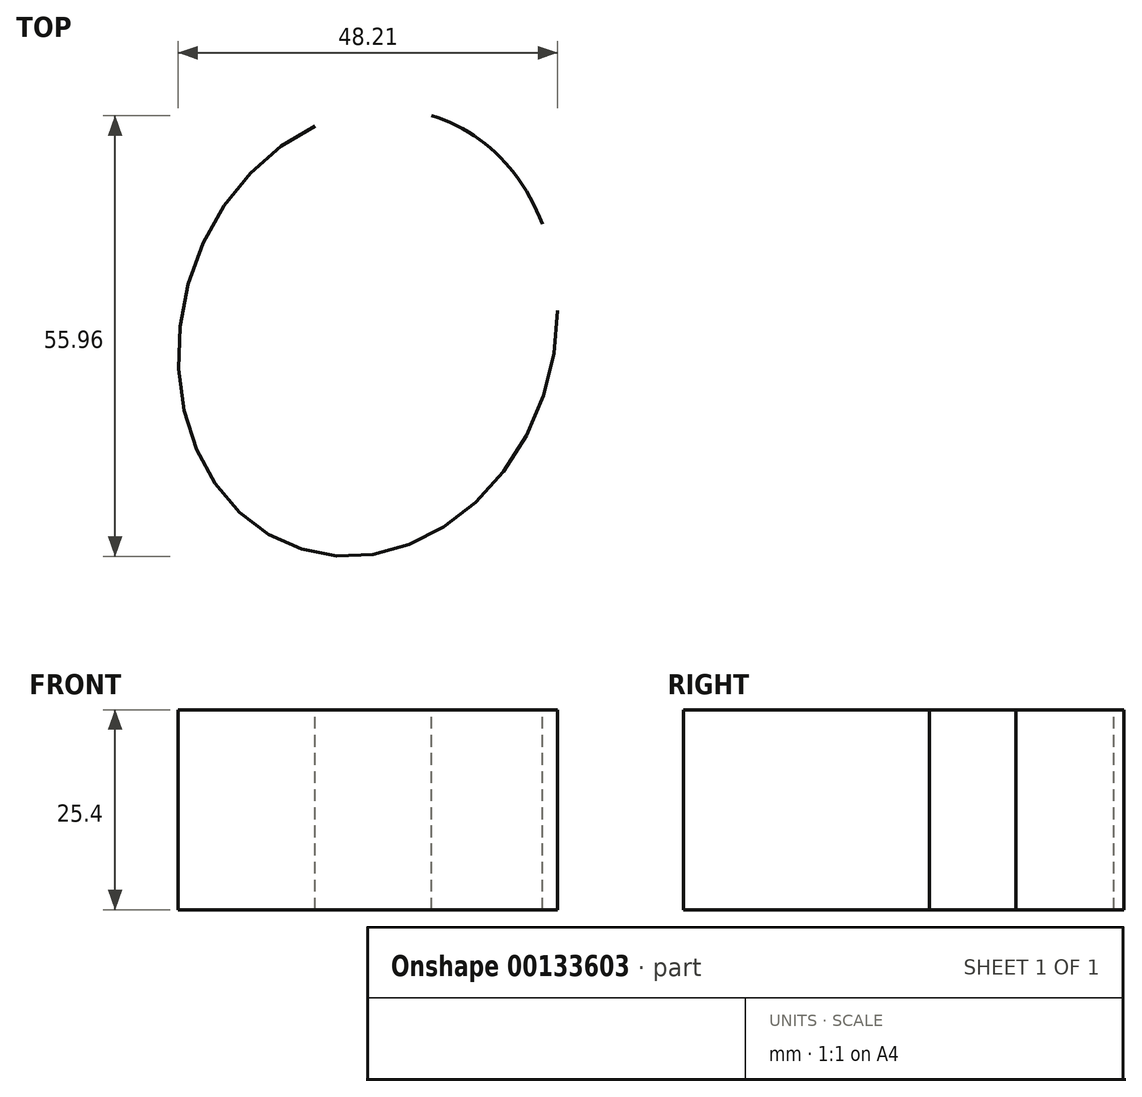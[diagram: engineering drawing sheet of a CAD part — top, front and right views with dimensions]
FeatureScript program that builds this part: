
annotation { "Feature Type Name" : "Feature", "Feature Type Description" : "" }
export const myFeature = defineFeature(function(context is Context, id is Id, definition is map)
    precondition{}
    {
        {
            var Q0;
            Q0=qCreatedBy(makeId("Top.planeOp"),FACE);
            var sketch = newSketch(context, id + "F0", { "sketchPlane" : qUnion([Q0])});
            skEllipticalArc(sketch, "E0", {});
            skPoint(sketch, "E1.2.internal.snap0", {"position": v(-56.5, -27.58) * mm});
            skEllipticalArc(sketch, "E2.trimOffspring", {});
            const initialGuessF0  = {"E0": [-0.04839024506509304, 0, 0.9594307271229442, -0.2819444623544479, 0.023661924534453375, 0.028747353709748735, 0.7455307443267936, 1.5707963267948966], "E2.trimOffspring": [-0.04839024506509304, 0, 0.9594307271229442, -0.2819444623544479, 0.023661924534453375, 0.028747353709748735, 2.1958314821106333, 0.3374060144198605]};
            skSetInitialGuess(sketch, initialGuessF0);
            skSolve(sketch);
        }
        {
            var Q0;
            Q0=sQuery(id+"F0.wireOp",EDGE,"E0");
            var Q1;
            Q1=sQuery(id+"F0.wireOp",EDGE,"E2.trimOffspring");
            extrude(context, id + "F1", {"bodyType" : ToolBodyType.SURFACE, "surfaceEntities" : qUnion([Q0, Q1]), "depth" : 25.4 * mm});
        }
    });
